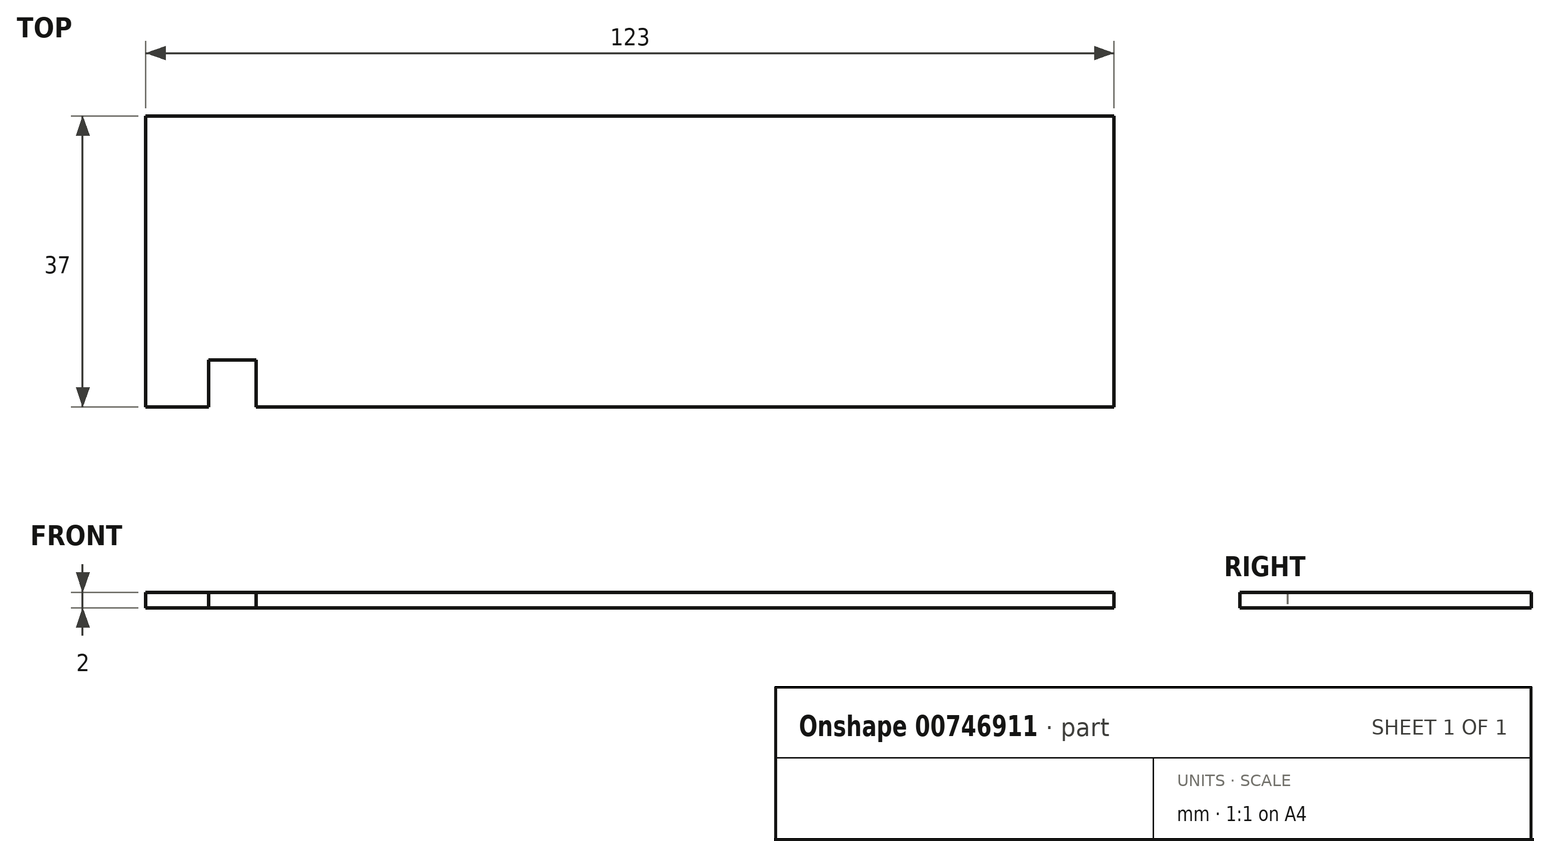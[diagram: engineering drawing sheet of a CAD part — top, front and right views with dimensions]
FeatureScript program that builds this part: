
annotation { "Feature Type Name" : "Feature", "Feature Type Description" : "" }
export const myFeature = defineFeature(function(context is Context, id is Id, definition is map)
    precondition{}
    {
        {
            var Q0;
            Q0=qCreatedBy(makeId("Top.planeOp"),FACE);
            var sketch = newSketch(context, id + "F0", { "sketchPlane" : qUnion([Q0])});
            skLineSegment(sketch, "E0", {"start": v(0, 0) * mm, "end": v(0, 37) * mm});
            skLineSegment(sketch, "E1", {"start": v(0, 37) * mm, "end": v(123, 37) * mm});
            skLineSegment(sketch, "E2", {"start": v(123, 37) * mm, "end": v(123, 0) * mm});
            skLineSegment(sketch, "E3", {"start": v(123, 0) * mm, "end": v(14, 0) * mm});
            skLineSegment(sketch, "E4", {"start": v(14, 0) * mm, "end": v(14, 6) * mm});
            skLineSegment(sketch, "E5", {"start": v(14, 6) * mm, "end": v(8, 6) * mm});
            skLineSegment(sketch, "E6", {"start": v(8, 6) * mm, "end": v(8, 0) * mm});
            skLineSegment(sketch, "E7", {"start": v(8, 0) * mm, "end": v(0, 0) * mm});
            skSolve(sketch);
        }
        {
            var Q0;
            Q0 = qSketchRegion(id + "F0", true);
            extrude(context, id + "F1", {"entities" : qUnion([Q0]), "depth" : 2 * mm, "offsetDistance" : 25 * mm});
        }
    });
